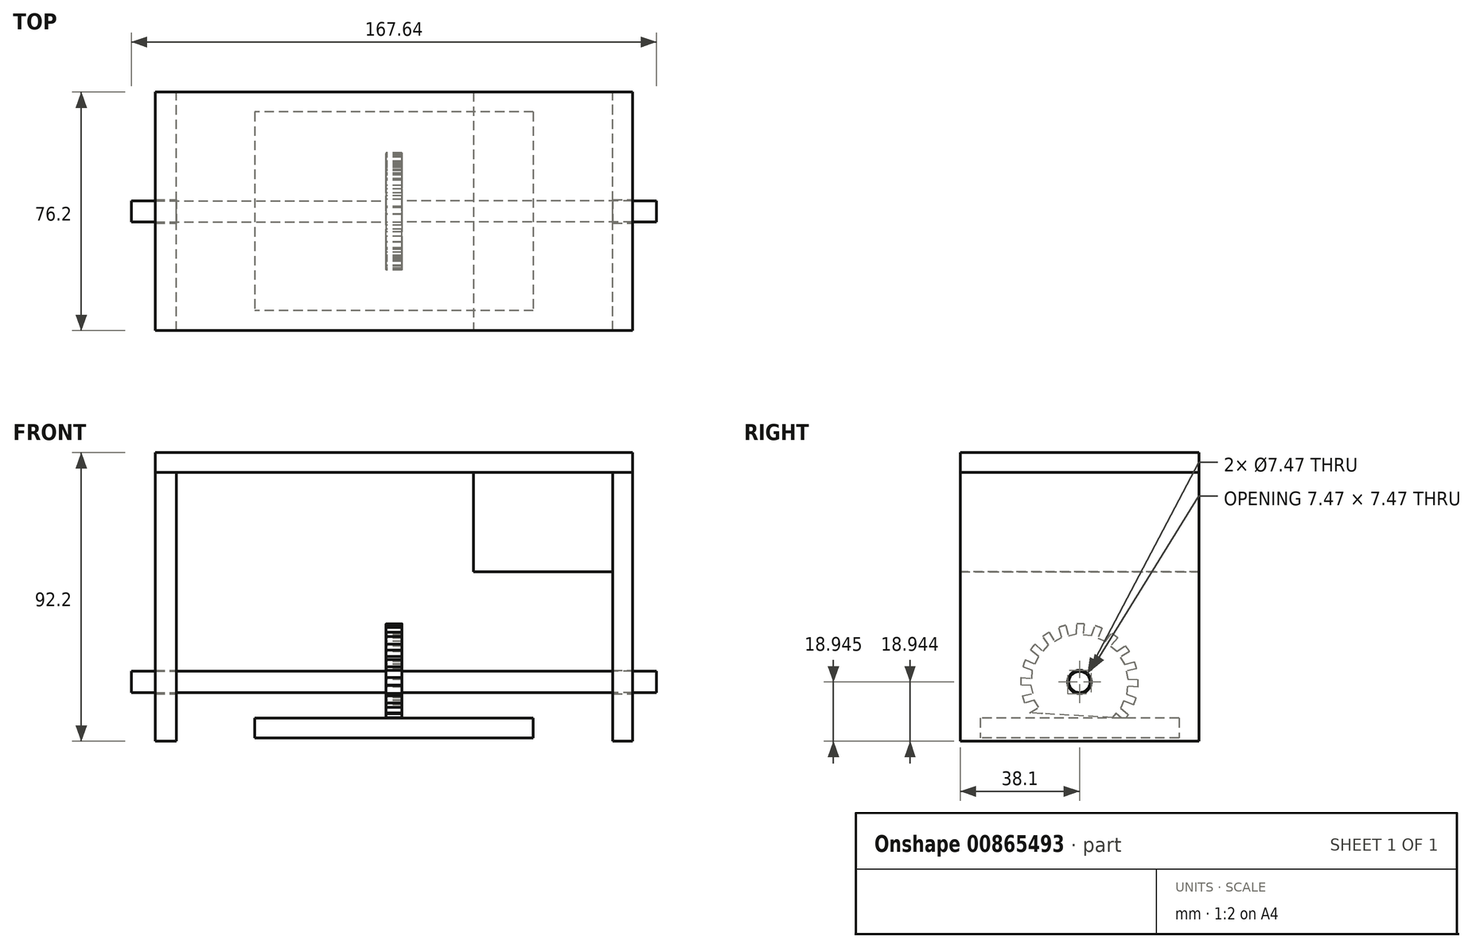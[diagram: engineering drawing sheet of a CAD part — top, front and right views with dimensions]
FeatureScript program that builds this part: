
annotation { "Feature Type Name" : "Feature", "Feature Type Description" : "" }
export const myFeature = defineFeature(function(context is Context, id is Id, definition is map)
    precondition{}
    {
        {
            var Q0;
            Q0=qCreatedBy(makeId("Top.planeOp"),FACE);
            var sketch = newSketch(context, id + "F0", { "sketchPlane" : qUnion([Q0])});
            skLineSegment(sketch, "E0.bottom", {"start": v(-69.85, 38.1) * mm, "end": v(69.44, 38.1) * mm});
            skLineSegment(sketch, "E0.top", {"start": v(-69.44, -38.1) * mm, "end": v(69.85, -38.1) * mm});
            skPoint(sketch, "E0.middle", {"position": v(0, 0) * mm});
            skLineSegment(sketch, "E1.bottom", {"start": v(-76.2, 38.1) * mm, "end": v(76.2, 38.1) * mm});
            skLineSegment(sketch, "E1.right", {"start": v(76.2, 38.1) * mm, "end": v(76.2, -38.1) * mm});
            skLineSegment(sketch, "E2.bottom", {"start": v(-76.2, 38.1) * mm, "end": v(-58.42, 38.1) * mm});
            skLineSegment(sketch, "E2.top", {"start": v(-76.2, -38.1) * mm, "end": v(-69.44, -38.1) * mm});
            skLineSegment(sketch, "E2.left", {"start": v(-76.2, 38.1) * mm, "end": v(-76.2, -38.1) * mm});
            skLineSegment(sketch, "E3.bottom", {"start": v(69.44, 38.1) * mm, "end": v(76.2, 38.1) * mm});
            skLineSegment(sketch, "E3.top", {"start": v(58.42, -38.1) * mm, "end": v(76.2, -38.1) * mm});
            skLineSegment(sketch, "E4.bottom", {"start": v(-69.44, -38.1) * mm, "end": v(-76.2, -38.1) * mm});
            skLineSegment(sketch, "E4.top", {"start": v(-69.44, 38.1) * mm, "end": v(-76.2, 38.1) * mm});
            skLineSegment(sketch, "E4.left", {"start": v(-69.44, -38.1) * mm, "end": v(-69.44, 38.1) * mm});
            skLineSegment(sketch, "E4.right", {"start": v(-76.2, -38.1) * mm, "end": v(-76.2, 38.1) * mm});
            skLineSegment(sketch, "E5.bottom", {"start": v(69.85, -38.1) * mm, "end": v(76.2, -38.1) * mm});
            skLineSegment(sketch, "E5.top", {"start": v(69.85, 38.1) * mm, "end": v(76.2, 38.1) * mm});
            skLineSegment(sketch, "E5.left", {"start": v(69.85, -38.1) * mm, "end": v(69.85, 38.1) * mm});
            skLineSegment(sketch, "E5.right", {"start": v(76.2, -38.1) * mm, "end": v(76.2, 38.1) * mm});
            skLineSegment(sketch, "E6.top", {"start": v(-76.2, -38.1) * mm, "end": v(76.2, -38.1) * mm});
            skSolve(sketch);
        }
        {
            var Q0;
            {var subQ0=sQuery(id+"F0.wireOp",EDGE,"E4.left");Q0=makeQuery(id+"F0.imprint","IMPRINT",FACE,{"disambiguationData":[TD([[makeQuery(id+"F0.imprint","IMPRINT",EDGE,{"derivedFrom":subQ0}),1.0]])]});}
            var Q1;
            {var subQ0=sQuery(id+"F0.wireOp",EDGE,"E5.left");Q1=makeQuery(id+"F0.imprint","IMPRINT",FACE,{"disambiguationData":[TD([[makeQuery(id+"F0.imprint","IMPRINT",EDGE,{"derivedFrom":subQ0}),-1.0]])]});}
            extrude(context, id + "F1", {"entities" : qUnion([Q0, Q1]), "oppositeDirection" : true, "depth" : 85.85 * mm, "offsetDistance" : 25.4 * mm});
        }
        {
            var Q0;
            {var subQ0=sQuery(id+"F0.wireOp",EDGE,"E4.left");Q0=makeQuery(id+"F0.imprint","IMPRINT",FACE,{"disambiguationData":[TD([[makeQuery(id+"F0.imprint","IMPRINT",EDGE,{"derivedFrom":subQ0}),1.0]])]});}
            var Q1;
            {var subQ0=sQuery(id+"F0.wireOp",EDGE,"E4.left");Q1=makeQuery(id+"F0.imprint","IMPRINT",FACE,{"disambiguationData":[TD([[makeQuery(id+"F0.imprint","IMPRINT",EDGE,{"derivedFrom":subQ0}),-1.0]])]});}
            var Q2;
            {var subQ0=sQuery(id+"F0.wireOp",EDGE,"E5.left");Q2=makeQuery(id+"F0.imprint","IMPRINT",FACE,{"disambiguationData":[TD([[makeQuery(id+"F0.imprint","IMPRINT",EDGE,{"derivedFrom":subQ0}),-1.0]])]});}
            extrude(context, id + "F2", {"entities" : qUnion([Q0, Q1, Q2]), "depth" : 6.35 * mm, "offsetDistance" : 25.4 * mm});
        }
        {
            var Q0;
            Q0=qCreatedBy(makeId("Right.planeOp"),FACE);
            var sketch = newSketch(context, id + "F3", { "sketchPlane" : qUnion([Q0])});
            skCircle(sketch, "E7", {"center": v(0, -66.9) * mm, "radius": 3.74 * mm});
            skSolve(sketch);
        }
        {
            var Q0;
            Q0 = qSketchRegion(id + "F3", true);
            extrude(context, id + "F4", {"entities" : qUnion([Q0]), "operationType" : NewBodyOperationType.REMOVE, "endBound" : BoundingType.SYMMETRIC, "oppositeDirection" : true, "depth" : 254 * mm, "offsetDistance" : 25.4 * mm});
        }
        {
            var Q0;
            Q0=qCreatedBy(makeId("Top.planeOp"),FACE);
            var sketch = newSketch(context, id + "F5", { "sketchPlane" : qUnion([Q0])});
            skLineSegment(sketch, "E8", {"start": v(69.85, 38.1) * mm, "end": v(25.4, 38.1) * mm});
            skLineSegment(sketch, "E9", {"start": v(25.4, 38.1) * mm, "end": v(25.4, -37.97) * mm});
            skLineSegment(sketch, "E10", {"start": v(25.4, -37.97) * mm, "end": v(69.85, -37.97) * mm});
            skLineSegment(sketch, "E11", {"start": v(69.85, -37.97) * mm, "end": v(69.85, 38.1) * mm});
            skSolve(sketch);
        }
        {
            var Q0;
            Q0 = qSketchRegion(id + "F5", true);
            extrude(context, id + "F6", {"entities" : qUnion([Q0]), "oppositeDirection" : true, "depth" : 31.75 * mm, "offsetDistance" : 25.4 * mm});
        }
        {
            var Q0;
            Q0=qCreatedBy(makeId("Right.planeOp"),FACE);
            var sketch = newSketch(context, id + "F7", { "sketchPlane" : qUnion([Q0])});
            skCircle(sketch, "E12", {"center": v(0, -66.9) * mm, "radius": 3.4 * mm});
            skSolve(sketch);
        }
        {
            var Q0;
            Q0 = qSketchRegion(id + "F7", true);
            extrude(context, id + "F8", {"entities" : qUnion([Q0]), "depth" : 83.82 * mm, "offsetDistance" : 25.4 * mm});
        }
        {
            var Q0;
            Q0=makeQuery(id+"F8.opExtrude","SWEPT_BODY",BODY,{"disambiguationData":[OSD([sQuery(id+"F7.wireOp",EDGE,"E12")])]});
            var Q1;
            Q1=qCreatedBy(makeId("Right.planeOp"),FACE);
            mirror(context, id + "F9", {"operationType" : NewBodyOperationType.ADD, "entities" : qUnion([Q0]), "mirrorPlane" : qUnion([Q1])});
        }
        {
            var Q0;
            Q0=qCreatedBy(makeId("Right.planeOp"),FACE);
            var sketch = newSketch(context, id + "F10", { "sketchPlane" : qUnion([Q0])});
            skLineSegment(sketch, "E13.bottom", {"start": v(31.75, -78.5) * mm, "end": v(-31.75, -78.5) * mm});
            skLineSegment(sketch, "E13.top", {"start": v(31.75, -84.85) * mm, "end": v(-31.75, -84.85) * mm});
            skLineSegment(sketch, "E13.left", {"start": v(31.75, -78.5) * mm, "end": v(31.75, -84.85) * mm});
            skLineSegment(sketch, "E13.right", {"start": v(-31.75, -78.5) * mm, "end": v(-31.75, -84.85) * mm});
            skPoint(sketch, "E13.middle", {"position": v(0, -81.67) * mm});
            skSolve(sketch);
        }
        {
            var Q0;
            Q0 = qSketchRegion(id + "F10", true);
            extrude(context, id + "F11", {"entities" : qUnion([Q0]), "operationType" : NewBodyOperationType.ADD, "endBound" : BoundingType.SYMMETRIC, "depth" : 88.9 * mm, "offsetDistance" : 25.4 * mm});
        }
        {
            var Q0;
            Q0=qCreatedBy(makeId("Right.planeOp"),FACE);
            var sketch = newSketch(context, id + "F12", { "sketchPlane" : qUnion([Q0])});
            skArc(sketch, "E14", {"start": v(16.5, -75.88) * mm, "mid": v(-0.52, -48.3) * mm, "end": v(-15.99, -76.78) * mm});
            skFitSpline(sketch, "E15", {"points": [v(14.77, -78.54) * mm, v(-15.99, -76.78) * mm], "startDerivative": vector(-24.79, 1.42) * mm, "endDerivative": vector(-24.79, 1.42) * mm});
            skArc(sketch, "E16", {"start": v(16.5, -75.88) * mm, "mid": v(15.64, -77.2) * mm, "end": v(14.77, -78.54) * mm});
            skLineSegment(sketch, "E17", {"start": v(-15.99, -76.78) * mm, "end": v(-13.03, -75) * mm});
            skLineSegment(sketch, "E18", {"start": v(-13.03, -75) * mm, "end": v(-14.4, -72.72) * mm});
            skLineSegment(sketch, "E19", {"start": v(-14.4, -72.72) * mm, "end": v(-17.53, -73.62) * mm});
            skLineSegment(sketch, "E20.1.1", {"start": v(-11.8, -77.02) * mm, "end": v(-11.94, -76.9) * mm});
            skLineSegment(sketch, "E20.1.2", {"start": v(-11.94, -76.9) * mm, "end": v(-12.1, -77) * mm});
            skLineSegment(sketch, "E20.6.0", {"start": v(13.36, -78.46) * mm, "end": v(11.62, -76.95) * mm});
            skLineSegment(sketch, "E20.6.1", {"start": v(11.62, -76.95) * mm, "end": v(10.45, -78.3) * mm});
            skLineSegment(sketch, "E20.7.0", {"start": v(17.3, -74.22) * mm, "end": v(14.12, -72.87) * mm});
            skLineSegment(sketch, "E20.7.1", {"start": v(14.12, -72.87) * mm, "end": v(13.08, -75.32) * mm});
            skLineSegment(sketch, "E20.7.2", {"start": v(13.08, -75.32) * mm, "end": v(15.65, -77.32) * mm});
            skLineSegment(sketch, "E20.8.0", {"start": v(18.67, -68.52) * mm, "end": v(15.23, -68.22) * mm});
            skLineSegment(sketch, "E20.8.1", {"start": v(15.23, -68.22) * mm, "end": v(15, -70.87) * mm});
            skLineSegment(sketch, "E20.8.2", {"start": v(15, -70.87) * mm, "end": v(18.06, -71.98) * mm});
            skLineSegment(sketch, "E20.9.0", {"start": v(18.22, -62.68) * mm, "end": v(14.86, -63.46) * mm});
            skLineSegment(sketch, "E20.9.1", {"start": v(14.86, -63.46) * mm, "end": v(15.46, -66.05) * mm});
            skLineSegment(sketch, "E20.9.2", {"start": v(15.46, -66.05) * mm, "end": v(18.71, -66.16) * mm});
            skLineSegment(sketch, "E20.10.0", {"start": v(15.99, -57.26) * mm, "end": v(13.03, -59.04) * mm});
            skLineSegment(sketch, "E20.10.1", {"start": v(13.03, -59.04) * mm, "end": v(14.4, -61.32) * mm});
            skLineSegment(sketch, "E20.10.2", {"start": v(14.4, -61.32) * mm, "end": v(17.53, -60.42) * mm});
            skLineSegment(sketch, "E20.11.0", {"start": v(12.2, -52.8) * mm, "end": v(9.93, -55.4) * mm});
            skLineSegment(sketch, "E20.11.1", {"start": v(9.93, -55.4) * mm, "end": v(11.94, -57.14) * mm});
            skLineSegment(sketch, "E20.11.2", {"start": v(11.94, -57.14) * mm, "end": v(14.63, -55.32) * mm});
            skLineSegment(sketch, "E20.12.0", {"start": v(7.2, -49.72) * mm, "end": v(5.85, -52.9) * mm});
            skLineSegment(sketch, "E20.12.1", {"start": v(5.85, -52.9) * mm, "end": v(8.3, -53.94) * mm});
            skLineSegment(sketch, "E20.12.2", {"start": v(8.3, -53.94) * mm, "end": v(10.3, -51.37) * mm});
            skLineSegment(sketch, "E20.13.0", {"start": v(1.5, -48.35) * mm, "end": v(1.2, -51.79) * mm});
            skLineSegment(sketch, "E20.13.1", {"start": v(1.2, -51.79) * mm, "end": v(3.85, -52.01) * mm});
            skLineSegment(sketch, "E20.13.2", {"start": v(3.85, -52.01) * mm, "end": v(4.96, -48.96) * mm});
            skLineSegment(sketch, "E20.14.0", {"start": v(-4.34, -48.8) * mm, "end": v(-3.56, -52.16) * mm});
            skLineSegment(sketch, "E20.14.1", {"start": v(-3.56, -52.16) * mm, "end": v(-0.97, -51.56) * mm});
            skLineSegment(sketch, "E20.14.2", {"start": v(-0.97, -51.56) * mm, "end": v(-0.86, -48.3) * mm});
            skLineSegment(sketch, "E20.15.0", {"start": v(-9.76, -51.03) * mm, "end": v(-7.98, -53.99) * mm});
            skLineSegment(sketch, "E20.15.1", {"start": v(-7.98, -53.99) * mm, "end": v(-5.7, -52.61) * mm});
            skLineSegment(sketch, "E20.15.2", {"start": v(-5.7, -52.61) * mm, "end": v(-6.6, -49.49) * mm});
            skLineSegment(sketch, "E20.16.0", {"start": v(-14.22, -54.83) * mm, "end": v(-11.62, -57.09) * mm});
            skLineSegment(sketch, "E20.16.1", {"start": v(-11.62, -57.09) * mm, "end": v(-9.88, -55.08) * mm});
            skLineSegment(sketch, "E20.16.2", {"start": v(-9.88, -55.08) * mm, "end": v(-11.7, -52.38) * mm});
            skLineSegment(sketch, "E20.17.0", {"start": v(-17.3, -59.82) * mm, "end": v(-14.12, -61.16) * mm});
            skLineSegment(sketch, "E20.17.1", {"start": v(-14.12, -61.16) * mm, "end": v(-13.08, -58.72) * mm});
            skLineSegment(sketch, "E20.17.2", {"start": v(-13.08, -58.72) * mm, "end": v(-15.65, -56.71) * mm});
            skLineSegment(sketch, "E20.18.0", {"start": v(-18.67, -65.52) * mm, "end": v(-15.23, -65.81) * mm});
            skLineSegment(sketch, "E20.18.1", {"start": v(-15.23, -65.81) * mm, "end": v(-15, -63.17) * mm});
            skLineSegment(sketch, "E20.18.2", {"start": v(-15, -63.17) * mm, "end": v(-18.06, -62.05) * mm});
            skLineSegment(sketch, "E20.19.0", {"start": v(-18.22, -71.36) * mm, "end": v(-14.86, -70.58) * mm});
            skLineSegment(sketch, "E20.19.1", {"start": v(-14.86, -70.58) * mm, "end": v(-15.46, -68) * mm});
            skLineSegment(sketch, "E20.19.2", {"start": v(-15.46, -68) * mm, "end": v(-18.71, -67.88) * mm});
            skPoint(sketch, "E21.orphan", {"position": v(-9.93, -78.63) * mm});
            skPoint(sketch, "E22.orphan", {"position": v(-14.63, -78.71) * mm});
            skPoint(sketch, "E23.orphan", {"position": v(9.88, -78.95) * mm});
            skPoint(sketch, "E24.orphan", {"position": v(14.22, -79.2) * mm});
            skSolve(sketch);
        }
        {
            var Q0;
            Q0=makeQuery(id+"F12.imprint","IMPRINT",FACE,{"disambiguationData":[TD([[makeQuery(id+"F12.imprint","IMPRINT",EDGE,{"derivedFrom":sQuery(id+"F12.wireOp",EDGE,"E14")}),1.0]])]});
            extrude(context, id + "F13", {"entities" : qUnion([Q0]), "operationType" : NewBodyOperationType.ADD, "endBound" : BoundingType.SYMMETRIC, "depth" : 5.08 * mm, "offsetDistance" : 25.4 * mm});
        }
    });
